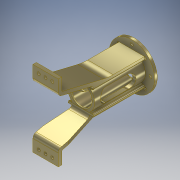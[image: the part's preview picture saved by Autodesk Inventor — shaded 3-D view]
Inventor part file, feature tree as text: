
AUTODESK INVENTOR PART (.ipt)
format: ipt  version: 2017 (Build 210142000, 142)  size: 344,576 bytes
history: native  units: mm
features: extrude x7, sketch x5, plane x4, mirror x2, fillet x2, projected_geometry x2
ambient origin geometry x8: Origin, YZ Plane, XZ Plane, XY Plane, X Axis, Y Axis, Z Axis, Center Point
bodies: Solid1 (feature_tree)
feature tree (22):
  sketch  "Sketch1"  dims[d1=80.0mm d2=54.0mm d3=28.0mm d4=32.0mm d5=24.0mm d6=44.0mm d7=3.5mm d8=360.0deg d9=15.556349mm d10=3.0mm d11=0.0mm]
  extrude  "Extrusion1"  Depth=3.0mm TaperAngle=0.0deg
  extrude  "Extrusion3"  Depth=60.0mm TaperAngle=0.0deg
  extrude  "Extrusion4"  Depth=2.0mm TaperAngle=0.0deg
  plane  "Work Plane1"
  plane  "Work Plane2"
  extrude  "Extrusion5"  Depth=2.0mm
  plane  "Work Plane8"
  extrude  "Extrusion7"  Depth=2.0mm
  extrude  "Extrusion8"  Depth=2.0mm
  mirror  "Mirror1"
  mirror  "Mirror2"
  fillet  "Fillet1"  Radius=89.9mm
  plane  "Work Plane9"
  extrude  "Extrusion9"  Depth=2.0mm
  fillet  "Fillet2"  Radius=44.2mm
  sketch  "Sketch4"  dims[d14=60.0mm d15=0.0mm d16=1.0mm d17=0.0mm]
  sketch  "Sketch9"  dims[d18=0.0mm d19=0.0mm]
  projected_geometry  "Projected Loop1"
  projected_geometry  "Projected Loop2"
  sketch  "Sketch10"  dims[d20=18.0mm d21=43.0mm d22=4.0mm d23=2.0mm d24=5.0mm d25=50.0mm d26=2.347726mm d27=29.078495mm d28=33.0mm d29=5.0mm d30=38.0mm d31=30.0mm d32=0.0mm]
  sketch  "Sketch12"  dims[d72=-55.0mm d85=7.0mm d86=7.0mm d87=89.9mm d88=89.9mm d89=44.2mm d90=44.2mm d93=40.0mm d94=0.0mm d95=3.5mm d96=3.5mm d97=6.0mm d98=6.0mm d99=6.0mm d100=9.219544mm d101=16.155494mm d102=23.769729mm d103=45.0mm d104=45.0mm d105=47.434165mm d106=0.0mm d107=47.434165mm d108=0.0mm d109=0.0mm d110=1.0mm d111=34.0mm d113=16.0mm d114=26.0mm d115=8.0mm d116=8.0mm d117=0.0mm d118=20.615528mm d119=10.0mm d120=0.0mm d121=2.0mm]
